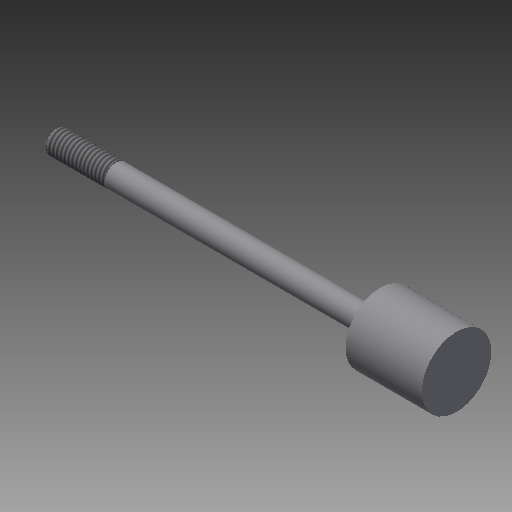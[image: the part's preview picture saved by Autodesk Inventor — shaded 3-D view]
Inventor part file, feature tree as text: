
AUTODESK INVENTOR PART (.ipt)
format: ipt  version: 2018 (Build 220112000, 112)  size: 156,160 bytes
history: native  units: in
note: dims shown in document units (in); Inventor stores cm internally (conversion verified against a paired STEP export)
features: other x70, revolve x3, sketch x3, thread x1
ambient origin geometry x8: Origin, YZ Plane, XZ Plane, XY Plane, X Axis, Y Axis, Z Axis, Center Point
bodies: Solid1 (feature_tree)
feature tree (77):
  revolve  "Revolution1"  Angle=360.0deg
  revolve  "Revolution2"  Angle=360.0deg
  thread  "Thread1"  [1 undecoded]
  revolve  "Revolution3"  [1 undecoded]
  other  "dia1_XY"
  other  "dia1_YZ"
  other  "dia1_ZX"
  other  "dia1_X"
  other  "dia1_Y"
  other  "dia1_Z"
  other  "dia1_Center"
  other  "dia12_XY"
  other  "dia12_YZ"
  other  "dia12_ZX"
  other  "dia12_X"
  other  "dia12_Y"
  other  "dia12_Z"
  other  "dia12_Center"
  other  "dia2_XY"
  other  "dia2_YZ"
  other  "dia2_ZX"
  other  "dia2_X"
  other  "dia2_Y"
  other  "dia2_Z"
  other  "dia2_Center"
  other  "dia22_XY"
  other  "dia22_YZ"
  other  "dia22_ZX"
  other  "dia22_X"
  other  "dia22_Y"
  other  "dia22_Z"
  other  "dia22_Center"
  other  "rl1_XY"
  other  "rl1_YZ"
  other  "rl1_ZX"
  other  "rl1_X"
  other  "rl1_Y"
  other  "rl1_Z"
  other  "rl1_Center"
  other  "rl2_XY"
  other  "rl2_YZ"
  other  "rl2_ZX"
  other  "rl2_X"
  other  "rl2_Y"
  other  "rl2_Z"
  other  "rl2_Center"
  other  "rod_cp_XY"
  other  "rod_cp_YZ"
  other  "rod_cp_ZX"
  other  "rod_cp_X"
  other  "rod_cp_Y"
  other  "rod_cp_Z"
  other  "rod_cp_Center"
  other  "thd1_XY"
  other  "thd1_YZ"
  other  "thd1_ZX"
  other  "thd1_X"
  other  "thd1_Y"
  other  "thd1_Z"
  other  "thd1_Center"
  other  "thd2_XY"
  other  "thd2_YZ"
  other  "thd2_ZX"
  other  "thd2_X"
  other  "thd2_Y"
  other  "thd2_Z"
  other  "thd2_Center"
  other  "to_rod_clevis_XY"
  other  "to_rod_clevis_YZ"
  other  "to_rod_clevis_ZX"
  other  "to_rod_clevis_X"
  other  "to_rod_clevis_Y"
  other  "to_rod_clevis_Z"
  other  "to_rod_clevis_Center"
  sketch  "Sketch_1"  dims[d0=360.0deg d1=360.0deg]
  sketch  "Sketch_3"  dims[d2=0.4814in d3=0.0in d4=360.0deg]
  sketch  "Sketch_30"  dims[d5=0.0in d6=0.0in d7=0.0in d8=0.0in d9=0.0in d10=0.0in]
note: 2 required parameter values undecoded (feature->parameter linkage not recoverable at this tier; creation-order binding heuristic only, values carry confidence <= 0.55)
